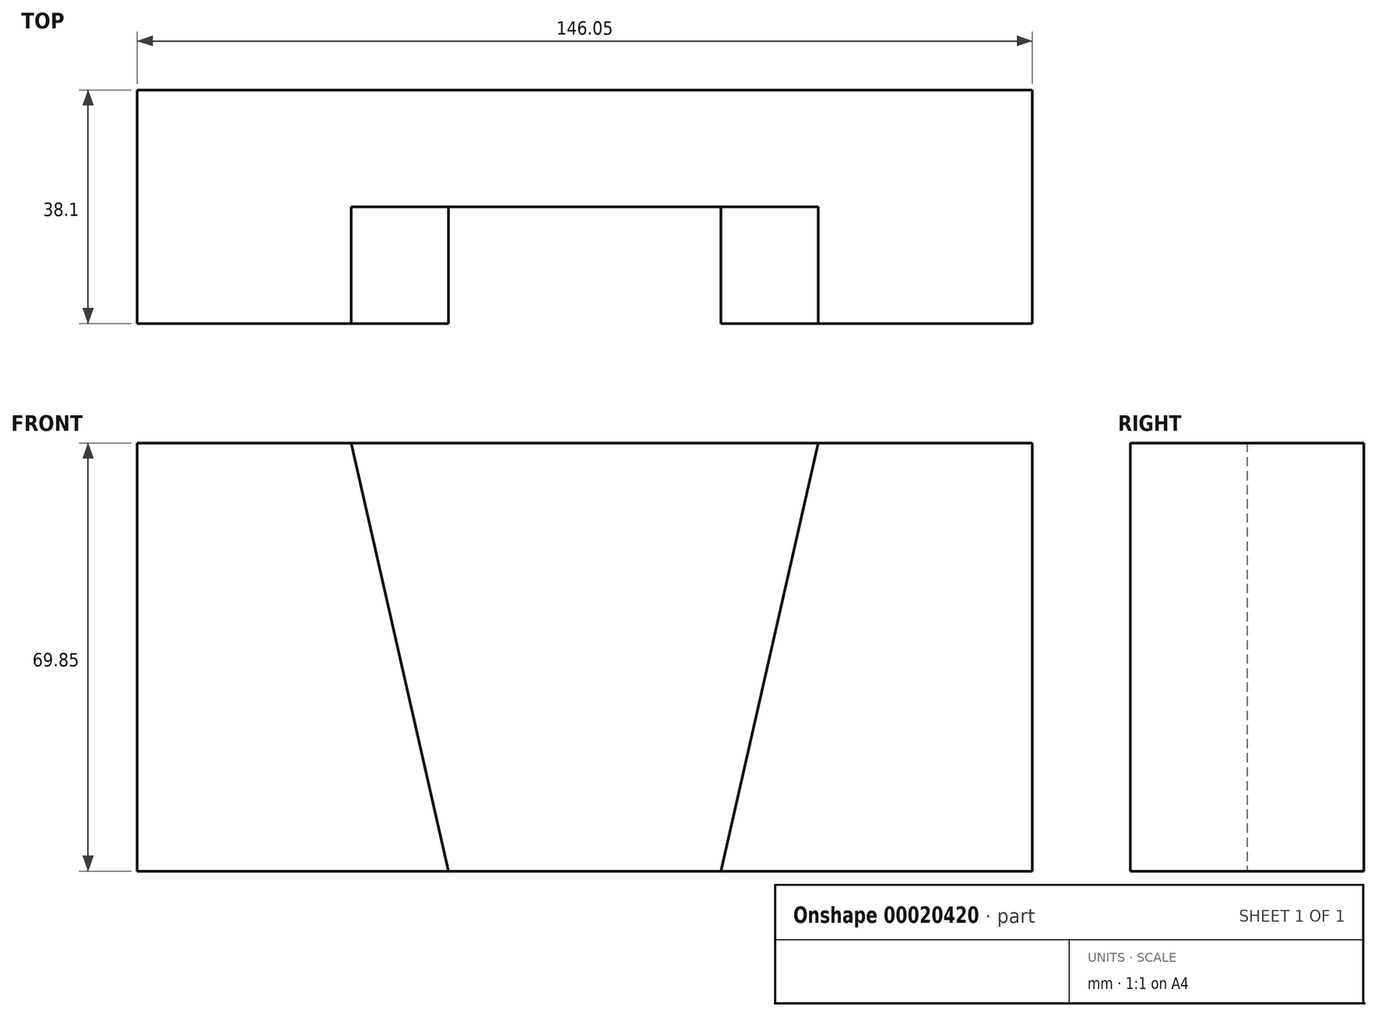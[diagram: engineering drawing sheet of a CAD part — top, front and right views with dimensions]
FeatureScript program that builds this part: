
annotation { "Feature Type Name" : "Feature", "Feature Type Description" : "" }
export const myFeature = defineFeature(function(context is Context, id is Id, definition is map)
    precondition{}
    {
        {
            var Q0;
            Q0=qCreatedBy(makeId("Front.planeOp"),FACE);
            var sketch = newSketch(context, id + "F0", { "sketchPlane" : qUnion([Q0])});
            skLineSegment(sketch, "E0.left", {"start": v(-67.2, 24.91) * mm, "end": v(-67.2, -44.94) * mm});
            skLineSegment(sketch, "E0.right", {"start": v(78.85, 24.91) * mm, "end": v(78.85, -44.94) * mm});
            skLineSegment(sketch, "E1", {"start": v(-67.2, 24.91) * mm, "end": v(-32.27, 24.91) * mm});
            skLineSegment(sketch, "E2", {"start": v(78.85, 24.91) * mm, "end": v(43.93, 24.91) * mm});
            skLineSegment(sketch, "E3", {"start": v(-67.2, -44.94) * mm, "end": v(-16.4, -44.94) * mm});
            skLineSegment(sketch, "E4", {"start": v(78.85, -44.94) * mm, "end": v(28.05, -44.94) * mm});
            skLineSegment(sketch, "E5", {"start": v(43.93, 24.91) * mm, "end": v(28.05, -44.94) * mm});
            skLineSegment(sketch, "E6", {"start": v(-32.27, 24.91) * mm, "end": v(-16.4, -44.94) * mm});
            skLineSegment(sketch, "E7", {"start": v(-32.27, 24.91) * mm, "end": v(43.93, 24.91) * mm});
            skLineSegment(sketch, "E8", {"start": v(28.05, -44.94) * mm, "end": v(-16.4, -44.94) * mm});
            skSolve(sketch);
        }
        {
            var Q0;
            Q0=makeQuery(id+"F0.imprint","IMPRINT",FACE,{"disambiguationData":[TD([[makeQuery(id+"F0.imprint","IMPRINT",EDGE,{"derivedFrom":sQuery(id+"F0.wireOp",EDGE,"E0.left")}),1.0]])]});
            extrude(context, id + "F1", {"entities" : qUnion([Q0]), "depth" : 38.1 * mm});
        }
        {
            var Q0;
            Q0=makeQuery(id+"F0.imprint","IMPRINT",FACE,{"disambiguationData":[TD([[makeQuery(id+"F0.imprint","IMPRINT",EDGE,{"derivedFrom":sQuery(id+"F0.wireOp",EDGE,"E5")}),-1.0]])]});
            extrude(context, id + "F2", {"entities" : qUnion([Q0]), "operationType" : NewBodyOperationType.ADD, "depth" : 19.05 * mm});
        }
        {
            var Q0;
            Q0=makeQuery(id+"F0.imprint","IMPRINT",FACE,{"disambiguationData":[TD([[makeQuery(id+"F0.imprint","IMPRINT",EDGE,{"derivedFrom":sQuery(id+"F0.wireOp",EDGE,"E0.right")}),-1.0]])]});
            extrude(context, id + "F3", {"entities" : qUnion([Q0]), "operationType" : NewBodyOperationType.ADD, "depth" : 38.1 * mm});
        }
    });
